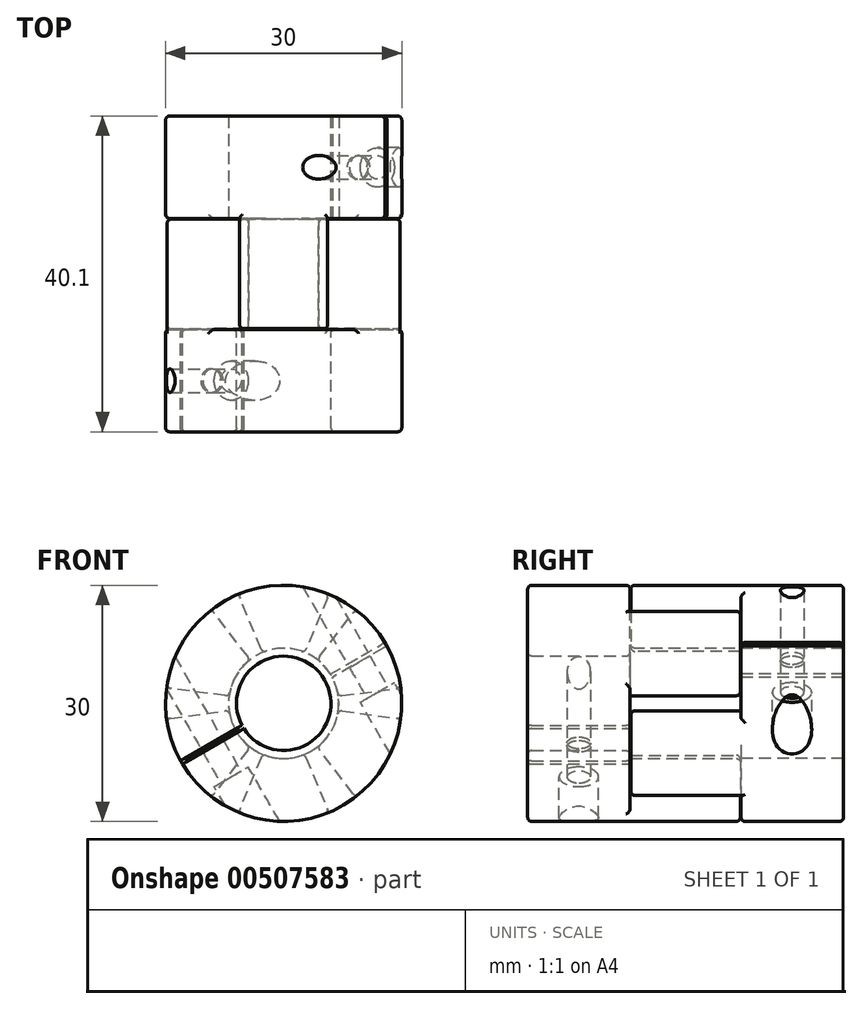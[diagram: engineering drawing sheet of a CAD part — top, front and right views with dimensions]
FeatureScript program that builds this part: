
annotation { "Feature Type Name" : "Feature", "Feature Type Description" : "" }
export const myFeature = defineFeature(function(context is Context, id is Id, definition is map)
    precondition{}
    {
        {
            var Q0;
            Q0=qCreatedBy(makeId("Front.planeOp"),FACE);
            var sketch = newSketch(context, id + "F0", { "sketchPlane" : qUnion([Q0])});
            skCircle(sketch, "E0", {"center": v(0, 0) * mm, "radius": 15 * mm});
            skSolve(sketch);
        }
        {
            var Q0;
            Q0=makeQuery(id+"F0.imprint","IMPRINT",FACE,{"disambiguationData":[TD([[makeQuery(id+"F0.imprint","IMPRINT",EDGE,{"derivedFrom":sQuery(id+"F0.wireOp",EDGE,"E0")}),1.0]])]});
            extrude(context, id + "F1", {"entities" : qUnion([Q0]), "depth" : 13 * mm});
        }
        {
            var Q0;
            Q0=makeQuery(id+"F1.opExtrude","CAP_FACE",FACE,{"disambiguationData":[OSD([sQuery(id+"F0.wireOp",EDGE,"E0")])],"isStart":false});
            var sketch = newSketch(context, id + "F2", { "sketchPlane" : qUnion([Q0])});
            skCircle(sketch, "E1", {"center": v(0, 0) * mm, "radius": 7 * mm});
            skSolve(sketch);
        }
        {
            var Q0;
            Q0=makeQuery(id+"F2.imprint","IMPRINT",FACE,{"disambiguationData":[TD([[makeQuery(id+"F2.imprint","IMPRINT",EDGE,{"derivedFrom":sQuery(id+"F2.wireOp",EDGE,"E1")}),1.0]])]});
            extrude(context, id + "F3", {"entities" : qUnion([Q0]), "operationType" : NewBodyOperationType.REMOVE, "oppositeDirection" : true, "depth" : 13 * mm});
        }
        {
            var Q0;
            Q0=makeQuery(id+"F1.opExtrude","CAP_FACE",FACE,{"disambiguationData":[OSD([sQuery(id+"F0.wireOp",EDGE,"E0")])],"isStart":false});
            var sketch = newSketch(context, id + "F4", { "sketchPlane" : qUnion([Q0])});
            skArc(sketch, "E2", {"start": v(2.68, 6.47) * mm, "mid": v(0, 7) * mm, "end": v(-2.68, 6.47) * mm});
            skArc(sketch, "E3", {"start": v(5.74, 13.86) * mm, "mid": v(0, 15) * mm, "end": v(-5.74, 13.86) * mm});
            skLineSegment(sketch, "E4", {"start": v(-2.68, 6.47) * mm, "end": v(-5.74, 13.86) * mm});
            skLineSegment(sketch, "E5", {"start": v(5.74, 13.86) * mm, "end": v(2.68, 6.47) * mm});
            skLineSegment(sketch, "E6.1.0", {"start": v(-4.26, -5.55) * mm, "end": v(-9.13, -11.9) * mm});
            skArc(sketch, "E6.1.1", {"start": v(-6.94, -0.91) * mm, "mid": v(-6.06, -3.5) * mm, "end": v(-4.26, -5.55) * mm});
            skArc(sketch, "E6.1.2", {"start": v(-14.87, -1.96) * mm, "mid": v(-13, -7.5) * mm, "end": v(-9.13, -11.9) * mm});
            skLineSegment(sketch, "E6.1.3", {"start": v(-14.87, -1.96) * mm, "end": v(-6.94, -0.91) * mm});
            skLineSegment(sketch, "E6.2.0", {"start": v(6.94, -0.91) * mm, "end": v(14.87, -1.96) * mm});
            skArc(sketch, "E6.2.1", {"start": v(4.26, -5.55) * mm, "mid": v(6.06, -3.5) * mm, "end": v(6.94, -0.91) * mm});
            skArc(sketch, "E6.2.2", {"start": v(9.13, -11.9) * mm, "mid": v(13, -7.5) * mm, "end": v(14.87, -1.96) * mm});
            skLineSegment(sketch, "E6.2.3", {"start": v(9.13, -11.9) * mm, "end": v(4.26, -5.55) * mm});
            skPoint(sketch, "E6.center", {"position": v(0, 0) * mm});
            skSolve(sketch);
        }
        {
            var Q0;
            Q0=makeQuery(id+"F4.imprint","IMPRINT",FACE,{"disambiguationData":[TD([[makeQuery(id+"F4.imprint","IMPRINT",EDGE,{"derivedFrom":sQuery(id+"F4.wireOp",EDGE,"E6.1.0")}),-1.0]])]});
            var Q1;
            Q1=makeQuery(id+"F4.imprint","IMPRINT",FACE,{"disambiguationData":[TD([[makeQuery(id+"F4.imprint","IMPRINT",EDGE,{"derivedFrom":sQuery(id+"F4.wireOp",EDGE,"E2")}),-1.0]])]});
            var Q2;
            Q2=makeQuery(id+"F4.imprint","IMPRINT",FACE,{"disambiguationData":[TD([[makeQuery(id+"F4.imprint","IMPRINT",EDGE,{"derivedFrom":sQuery(id+"F4.wireOp",EDGE,"E6.2.0")}),-1.0]])]});
            extrude(context, id + "F5", {"entities" : qUnion([Q0, Q1, Q2]), "operationType" : NewBodyOperationType.ADD, "depth" : 14 * mm});
        }
        {
            var Q0;
            Q0=makeQuery(id+"F5.opExtrude","CAP_EDGE",EDGE,{"disambiguationData":[OSD([sQuery(id+"F4.wireOp",EDGE,"E6.1.2")])],"isStart":false});
            var Q1;
            Q1=makeQuery(id+"F5.opExtrude","CAP_EDGE",EDGE,{"disambiguationData":[OSD([sQuery(id+"F4.wireOp",EDGE,"E6.1.0")])],"isStart":false});
            var Q2;
            Q2=makeQuery(id+"F5.opExtrude","CAP_EDGE",EDGE,{"disambiguationData":[OSD([sQuery(id+"F4.wireOp",EDGE,"E6.1.1")])],"isStart":false});
            var Q3;
            Q3=makeQuery(id+"F5.opExtrude","CAP_EDGE",EDGE,{"disambiguationData":[OSD([sQuery(id+"F4.wireOp",EDGE,"E6.1.3")])],"isStart":false});
            var Q4;
            Q4=makeQuery(id+"F5.opExtrude","SWEPT_EDGE",EDGE,{"disambiguationData":[OSD([sQuery(id+"F0.wireOp",EDGE,"E0"),sQuery(id+"F4.wireOp",EDGE,"E6.1.0"),sQuery(id+"F4.wireOp",EDGE,"E6.1.2")])]});
            var Q5;
            Q5=makeQuery(id+"F5.opExtrude","SWEPT_EDGE",EDGE,{"disambiguationData":[OSD([sQuery(id+"F0.wireOp",EDGE,"E0"),sQuery(id+"F4.wireOp",EDGE,"E6.1.2"),sQuery(id+"F4.wireOp",EDGE,"E6.1.3")])]});
            var Q6;
            Q6=makeQuery(id+"F5.opExtrude","SWEPT_EDGE",EDGE,{"disambiguationData":[OSD([sQuery(id+"F2.wireOp",EDGE,"E1"),sQuery(id+"F4.wireOp",EDGE,"E6.1.1"),sQuery(id+"F4.wireOp",EDGE,"E6.1.3")])]});
            var Q7;
            Q7=makeQuery(id+"F5.opExtrude","SWEPT_EDGE",EDGE,{"disambiguationData":[OSD([sQuery(id+"F2.wireOp",EDGE,"E1"),sQuery(id+"F4.wireOp",EDGE,"E6.1.0"),sQuery(id+"F4.wireOp",EDGE,"E6.1.1")])]});
            var Q8;
            {var subQ0=sQuery(id+"F2.wireOp",EDGE,"E1");Q8=makeQuery(id+"F5.boolean.opBoolean","SPLIT",EDGE,{"disambiguationData":[TD([makeQuery(id+"F5.opExtrude","SWEPT_FACE",FACE,{"disambiguationData":[OSD([sQuery(id+"F4.wireOp",EDGE,"E6.1.0")])]})])],"derivedFrom":makeQuery(id+"F3.boolean.opBoolean","COPY",EDGE,{"derivedFrom":makeQuery(id+"F3.opExtrude","CAP_EDGE",EDGE,{"disambiguationData":[OSD([subQ0])],"isStart":true})})});}
            var Q9;
            {var subQ0=sQuery(id+"F0.wireOp",EDGE,"E0");Q9=makeQuery(id+"F5.boolean.opBoolean","SPLIT",EDGE,{"disambiguationData":[TD([makeQuery(id+"F5.opExtrude","SWEPT_FACE",FACE,{"disambiguationData":[OSD([sQuery(id+"F4.wireOp",EDGE,"E6.1.0")])]})])],"derivedFrom":makeQuery(id+"F1.opExtrude","CAP_EDGE",EDGE,{"disambiguationData":[OSD([subQ0])],"isStart":false})});}
            var Q10;
            Q10=makeQuery(id+"F5.opExtrude","SWEPT_EDGE",EDGE,{"disambiguationData":[OSD([sQuery(id+"F2.wireOp",EDGE,"E1"),sQuery(id+"F4.wireOp",EDGE,"E6.2.1"),sQuery(id+"F4.wireOp",EDGE,"E6.2.3")])]});
            var Q11;
            Q11=makeQuery(id+"F5.opExtrude","CAP_EDGE",EDGE,{"disambiguationData":[OSD([sQuery(id+"F4.wireOp",EDGE,"E6.2.3")])],"isStart":false});
            var Q12;
            Q12=makeQuery(id+"F5.opExtrude","SWEPT_EDGE",EDGE,{"disambiguationData":[OSD([sQuery(id+"F0.wireOp",EDGE,"E0"),sQuery(id+"F4.wireOp",EDGE,"E6.2.2"),sQuery(id+"F4.wireOp",EDGE,"E6.2.3")])]});
            var Q13;
            Q13=makeQuery(id+"F5.opExtrude","CAP_EDGE",EDGE,{"disambiguationData":[OSD([sQuery(id+"F4.wireOp",EDGE,"E6.2.1")])],"isStart":false});
            var Q14;
            Q14=makeQuery(id+"F5.opExtrude","CAP_EDGE",EDGE,{"disambiguationData":[OSD([sQuery(id+"F4.wireOp",EDGE,"E6.2.2")])],"isStart":false});
            var Q15;
            Q15=makeQuery(id+"F5.opExtrude","SWEPT_EDGE",EDGE,{"disambiguationData":[OSD([sQuery(id+"F0.wireOp",EDGE,"E0"),sQuery(id+"F4.wireOp",EDGE,"E6.2.0"),sQuery(id+"F4.wireOp",EDGE,"E6.2.2")])]});
            var Q16;
            Q16=makeQuery(id+"F5.opExtrude","CAP_EDGE",EDGE,{"disambiguationData":[OSD([sQuery(id+"F4.wireOp",EDGE,"E6.2.0")])],"isStart":false});
            var Q17;
            Q17=makeQuery(id+"F5.opExtrude","SWEPT_EDGE",EDGE,{"disambiguationData":[OSD([sQuery(id+"F2.wireOp",EDGE,"E1"),sQuery(id+"F4.wireOp",EDGE,"E6.2.0"),sQuery(id+"F4.wireOp",EDGE,"E6.2.1")])]});
            var Q18;
            {var subQ0=sQuery(id+"F2.wireOp",EDGE,"E1");Q18=makeQuery(id+"F5.boolean.opBoolean","SPLIT",EDGE,{"disambiguationData":[TD([makeQuery(id+"F5.opExtrude","SWEPT_FACE",FACE,{"disambiguationData":[OSD([sQuery(id+"F4.wireOp",EDGE,"E5")])]})])],"derivedFrom":makeQuery(id+"F3.boolean.opBoolean","COPY",EDGE,{"derivedFrom":makeQuery(id+"F3.opExtrude","CAP_EDGE",EDGE,{"disambiguationData":[OSD([subQ0])],"isStart":true})})});}
            var Q19;
            {var subQ0=sQuery(id+"F0.wireOp",EDGE,"E0");Q19=makeQuery(id+"F5.boolean.opBoolean","SPLIT",EDGE,{"disambiguationData":[TD([makeQuery(id+"F5.opExtrude","SWEPT_FACE",FACE,{"disambiguationData":[OSD([sQuery(id+"F4.wireOp",EDGE,"E5")])]})])],"derivedFrom":makeQuery(id+"F1.opExtrude","CAP_EDGE",EDGE,{"disambiguationData":[OSD([subQ0])],"isStart":false})});}
            var Q20;
            Q20=makeQuery(id+"F5.opExtrude","SWEPT_EDGE",EDGE,{"disambiguationData":[OSD([sQuery(id+"F2.wireOp",EDGE,"E1"),sQuery(id+"F4.wireOp",EDGE,"E2"),sQuery(id+"F4.wireOp",EDGE,"E5")])]});
            var Q21;
            Q21=makeQuery(id+"F5.opExtrude","SWEPT_EDGE",EDGE,{"disambiguationData":[OSD([sQuery(id+"F0.wireOp",EDGE,"E0"),sQuery(id+"F4.wireOp",EDGE,"E3"),sQuery(id+"F4.wireOp",EDGE,"E5")])]});
            var Q22;
            Q22=makeQuery(id+"F5.opExtrude","CAP_EDGE",EDGE,{"disambiguationData":[OSD([sQuery(id+"F4.wireOp",EDGE,"E5")])],"isStart":false});
            var Q23;
            Q23=makeQuery(id+"F5.opExtrude","CAP_EDGE",EDGE,{"disambiguationData":[OSD([sQuery(id+"F4.wireOp",EDGE,"E2")])],"isStart":false});
            var Q24;
            Q24=makeQuery(id+"F5.opExtrude","CAP_EDGE",EDGE,{"disambiguationData":[OSD([sQuery(id+"F4.wireOp",EDGE,"E4")])],"isStart":false});
            var Q25;
            Q25=makeQuery(id+"F5.opExtrude","CAP_EDGE",EDGE,{"disambiguationData":[OSD([sQuery(id+"F4.wireOp",EDGE,"E3")])],"isStart":false});
            var Q26;
            Q26=makeQuery(id+"F5.opExtrude","SWEPT_EDGE",EDGE,{"disambiguationData":[OSD([sQuery(id+"F2.wireOp",EDGE,"E1"),sQuery(id+"F4.wireOp",EDGE,"E2"),sQuery(id+"F4.wireOp",EDGE,"E4")])]});
            var Q27;
            Q27=makeQuery(id+"F5.opExtrude","SWEPT_EDGE",EDGE,{"disambiguationData":[OSD([sQuery(id+"F0.wireOp",EDGE,"E0"),sQuery(id+"F4.wireOp",EDGE,"E3"),sQuery(id+"F4.wireOp",EDGE,"E4")])]});
            var Q28;
            {var subQ0=sQuery(id+"F0.wireOp",EDGE,"E0");Q28=makeQuery(id+"F5.boolean.opBoolean","SPLIT",EDGE,{"disambiguationData":[TD([makeQuery(id+"F5.opExtrude","SWEPT_FACE",FACE,{"disambiguationData":[OSD([sQuery(id+"F4.wireOp",EDGE,"E4")])]})])],"derivedFrom":makeQuery(id+"F1.opExtrude","CAP_EDGE",EDGE,{"disambiguationData":[OSD([subQ0])],"isStart":false})});}
            var Q29;
            {var subQ0=sQuery(id+"F2.wireOp",EDGE,"E1");Q29=makeQuery(id+"F5.boolean.opBoolean","SPLIT",EDGE,{"disambiguationData":[TD([makeQuery(id+"F5.opExtrude","SWEPT_FACE",FACE,{"disambiguationData":[OSD([sQuery(id+"F4.wireOp",EDGE,"E4")])]})])],"derivedFrom":makeQuery(id+"F3.boolean.opBoolean","COPY",EDGE,{"derivedFrom":makeQuery(id+"F3.opExtrude","CAP_EDGE",EDGE,{"disambiguationData":[OSD([subQ0])],"isStart":true})})});}
            fillet(context, id + "F6", {"entities" : qUnion([Q0, Q1, Q2, Q3, Q4, Q5, Q6, Q7, Q8, Q9, Q10, Q11, Q12, Q13, Q14, Q15, Q16, Q17, Q18, Q19, Q20, Q21, Q22, Q23, Q24, Q25, Q26, Q27, Q28, Q29]), "radius" : 0.5 * mm, "tangentPropagation" : true, "allowEdgeOverflow" : false});
        }
        {
            var Q0;
            Q0=makeQuery(id+"F3.boolean.opBoolean","COPY",EDGE,{"derivedFrom":makeQuery(id+"F3.opExtrude","CAP_EDGE",EDGE,{"disambiguationData":[OSD([sQuery(id+"F2.wireOp",EDGE,"E1")])],"isStart":false})});
            var Q1;
            Q1=makeQuery(id+"F1.opExtrude","CAP_EDGE",EDGE,{"disambiguationData":[OSD([sQuery(id+"F0.wireOp",EDGE,"E0")])],"isStart":true});
            fillet(context, id + "F7", {"entities" : qUnion([Q0, Q1]), "radius" : 0.5 * mm, "tangentPropagation" : true, "allowEdgeOverflow" : false});
        }
        {
            var Q0;
            {var subQ0=sQuery(id+"F0.wireOp",EDGE,"E0");Q0=makeQuery(id+"F5.boolean.opBoolean","SPLIT",FACE,{"disambiguationData":[TD([makeQuery(id+"F5.opExtrude","SWEPT_FACE",FACE,{"disambiguationData":[OSD([sQuery(id+"F4.wireOp",EDGE,"E5")])]})])],"derivedFrom":makeQuery(id+"F1.opExtrude","CAP_FACE",FACE,{"disambiguationData":[OSD([subQ0])],"isStart":false})});}
            var sketch = newSketch(context, id + "F8", { "sketchPlane" : qUnion([Q0])});
            skLineSegment(sketch, "E7", {"start": v(0, 0) * mm, "end": v(4.34, 2.5) * mm});
            skLineSegment(sketch, "E8", {"start": v(13.7, 7.91) * mm, "end": v(13.83, 7.7) * mm});
            skLineSegment(sketch, "E9", {"start": v(13.83, 7.7) * mm, "end": v(13.58, 8.13) * mm});
            skLineSegment(sketch, "E10", {"start": v(7.44, -0.98) * mm, "end": v(14.38, -1.9) * mm});
            skLineSegment(sketch, "E11", {"start": v(14.38, -1.9) * mm, "end": v(10.09, 5.54) * mm});
            skLineSegment(sketch, "E12", {"start": v(5.55, 13.4) * mm, "end": v(2.87, 6.93) * mm});
            skLineSegment(sketch, "E13", {"start": v(13.83, 7.7) * mm, "end": v(4.46, 2.29) * mm});
            skLineSegment(sketch, "E14", {"start": v(4.21, 2.72) * mm, "end": v(13.58, 8.13) * mm});
            skLineSegment(sketch, "E15", {"start": v(4.21, 2.72) * mm, "end": v(4.46, 2.29) * mm});
            skLineSegment(sketch, "E16.trimOffspring", {"start": v(9.84, 5.97) * mm, "end": v(5.55, 13.4) * mm});
            skSolve(sketch);
        }
        {
            var Q0;
            {var subQ20=sQuery(id+"F8.wireOp",EDGE,"E13");var subQ22=makeQuery(id+"F8.imprint","INTERSECT",VERTEX,{"derivedFrom":[sQuery(id+"F8.wireOp",EDGE,"E11"),subQ20]});Q0=makeQuery(id+"F8.imprint","IMPRINT",FACE,{"disambiguationData":[TD([[makeQuery(id+"F8.imprint","IMPRINT",EDGE,{"disambiguationData":[TD([[subQ22,1.0]])],"derivedFrom":subQ20}),-1.0]])]});}
            var Q1;
            {var subQ0=sQuery(id+"F8.wireOp",EDGE,"E13");var subQ1=sQuery(id+"F8.wireOp",EDGE,"E9");var subQ2=makeQuery(id+"F8.imprint","INTERSECT",VERTEX,{"derivedFrom":[subQ1,subQ0]});Q1=makeQuery(id+"F8.imprint","IMPRINT",FACE,{"disambiguationData":[TD([[makeQuery(id+"F8.imprint","IMPRINT",EDGE,{"disambiguationData":[TD([[subQ2,-1.0]])],"derivedFrom":subQ1}),1.0]])]});}
            var Q2;
            {var subQ0=sQuery(id+"F8.wireOp",EDGE,"E15");var subQ1=makeQuery(id+"F8.imprint","IMPRINT",VERTEX,{"derivedFrom":subQ0});Q2=makeQuery(id+"F8.imprint","IMPRINT",FACE,{"disambiguationData":[TD([[makeQuery(id+"F8.imprint","IMPRINT",EDGE,{"disambiguationData":[TD([[subQ1,1.0]])],"derivedFrom":subQ0}),1.0]])]});}
            extrude(context, id + "F9", {"entities" : qUnion([Q0, Q1, Q2]), "operationType" : NewBodyOperationType.REMOVE, "oppositeDirection" : true, "depth" : 13 * mm});
        }
        {
            var Q0;
            Q0=makeQuery(id+"F9.boolean.opBoolean","COPY",FACE,{"derivedFrom":makeQuery(id+"F9.opExtrude","SWEPT_FACE",FACE,{"disambiguationData":[OSD([sQuery(id+"F8.wireOp",EDGE,"E14")])]})});
            var sketch = newSketch(context, id + "F10", { "sketchPlane" : qUnion([Q0])});
            skLineSegment(sketch, "E17.bottom", {"start": v(7.5, 0) * mm, "end": v(14.5, 0) * mm});
            skLineSegment(sketch, "E17.top", {"start": v(7.5, 13) * mm, "end": v(14.5, 13) * mm});
            skLineSegment(sketch, "E17.left", {"start": v(7.5, 0) * mm, "end": v(7.5, 13) * mm});
            skLineSegment(sketch, "E17.right", {"start": v(14.5, 0) * mm, "end": v(14.5, 13) * mm});
            skCircle(sketch, "E18", {"center": v(11, 6.5) * mm, "radius": 1.5 * mm});
            skSolve(sketch);
        }
        {
            var Q0;
            Q0=makeQuery(id+"F10.imprint","IMPRINT",FACE,{"disambiguationData":[TD([[makeQuery(id+"F10.imprint","IMPRINT",EDGE,{"derivedFrom":sQuery(id+"F10.wireOp",EDGE,"E18")}),1.0]])]});
            extrude(context, id + "F11", {"entities" : qUnion([Q0]), "operationType" : NewBodyOperationType.REMOVE, "oppositeDirection" : true, "depth" : 25 * mm, "symmetric" : true});
        }
        {
            var Q0;
            Q0=makeQuery(id+"F9.boolean.opBoolean","COPY",FACE,{"derivedFrom":makeQuery(id+"F9.opExtrude","SWEPT_FACE",FACE,{"disambiguationData":[OSD([sQuery(id+"F8.wireOp",EDGE,"E14")])]})});
            cPlane(context, id + "F12", {"entities" : qUnion([Q0]), "cplaneType" : CPlaneType.OFFSET, "offset" : 5 * mm, "width" : 150 * mm, "height" : 150 * mm});
        }
        {
            var Q0;
            Q0=qCreatedBy(id+"F12.planeOp",FACE);
            var sketch = newSketch(context, id + "F13", { "sketchPlane" : qUnion([Q0])});
            skCircle(sketch, "E19", {"center": v(11, 6.53) * mm, "radius": 2.5 * mm});
            skSolve(sketch);
        }
        {
            var Q0;
            Q0=makeQuery(id+"F13.imprint","IMPRINT",FACE,{"disambiguationData":[TD([[makeQuery(id+"F13.imprint","IMPRINT",EDGE,{"derivedFrom":sQuery(id+"F13.wireOp",EDGE,"E19")}),1.0]])]});
            extrude(context, id + "F14", {"entities" : qUnion([Q0]), "operationType" : NewBodyOperationType.REMOVE, "depth" : 25 * mm});
        }
        {
            var Q0;
            {var subQ0=makeQuery(id+"F5.opExtrude","SWEPT_FACE",FACE,{"disambiguationData":[OSD([sQuery(id+"F4.wireOp",EDGE,"E5")])]});var subQ5=sQuery(id+"F0.wireOp",EDGE,"E0");var subQ6=makeQuery(id+"F1.opExtrude","CAP_FACE",FACE,{"disambiguationData":[OSD([subQ5])],"isStart":false});var subQ8=sQuery(id+"F4.wireOp",EDGE,"E6.2.0");var subQ9=makeQuery(id+"F5.opExtrude","SWEPT_FACE",FACE,{"disambiguationData":[OSD([subQ8])]});Q0=makeQuery(id+"F9.boolean.opBoolean","SPLIT",FACE,{"disambiguationData":[TD([subQ9])],"derivedFrom":makeQuery(id+"F5.boolean.opBoolean","SPLIT",FACE,{"disambiguationData":[TD([subQ0])],"derivedFrom":subQ6})});}
            cPlane(context, id + "F15", {"entities" : qUnion([Q0]), "cplaneType" : CPlaneType.OFFSET, "offset" : 0.1 * mm, "width" : 150 * mm, "height" : 150 * mm});
        }
        {
            var Q0;
            Q0=qCreatedBy(id+"F15.planeOp",FACE);
            var sketch = newSketch(context, id + "F16", { "sketchPlane" : qUnion([Q0])});
            skLineSegment(sketch, "E20", {"start": v(-2.68, -6.47) * mm, "end": v(-5.74, -13.86) * mm});
            skLineSegment(sketch, "E21", {"start": v(2.68, -6.47) * mm, "end": v(5.74, -13.86) * mm});
            skLineSegment(sketch, "E22", {"start": v(0, 0) * mm, "end": v(0, -7) * mm});
            skArc(sketch, "E23", {"start": v(-2.68, -6.47) * mm, "mid": v(0, -7) * mm, "end": v(2.68, -6.47) * mm});
            skArc(sketch, "E24", {"start": v(-5.74, -13.86) * mm, "mid": v(0, -15) * mm, "end": v(5.74, -13.86) * mm});
            skLineSegment(sketch, "E25.1.0", {"start": v(6.94, 0.91) * mm, "end": v(14.87, 1.96) * mm});
            skArc(sketch, "E25.1.1", {"start": v(6.94, 0.91) * mm, "mid": v(6.06, 3.5) * mm, "end": v(4.26, 5.55) * mm});
            skLineSegment(sketch, "E25.1.2", {"start": v(4.26, 5.55) * mm, "end": v(9.13, 11.9) * mm});
            skArc(sketch, "E25.1.3", {"start": v(14.87, 1.96) * mm, "mid": v(13, 7.5) * mm, "end": v(9.13, 11.9) * mm});
            skLineSegment(sketch, "E25.2.0", {"start": v(-4.26, 5.55) * mm, "end": v(-9.13, 11.9) * mm});
            skArc(sketch, "E25.2.1", {"start": v(-4.26, 5.55) * mm, "mid": v(-6.06, 3.5) * mm, "end": v(-6.94, 0.91) * mm});
            skLineSegment(sketch, "E25.2.2", {"start": v(-6.94, 0.91) * mm, "end": v(-14.87, 1.96) * mm});
            skArc(sketch, "E25.2.3", {"start": v(-9.13, 11.9) * mm, "mid": v(-13, 7.5) * mm, "end": v(-14.87, 1.96) * mm});
            skPoint(sketch, "E25.center", {"position": v(0, 0) * mm});
            skSolve(sketch);
        }
        {
            var Q0;
            Q0=makeQuery(id+"F16.imprint","IMPRINT",FACE,{"disambiguationData":[TD([[makeQuery(id+"F16.imprint","IMPRINT",EDGE,{"derivedFrom":sQuery(id+"F16.wireOp",EDGE,"E25.2.0")}),1.0]])]});
            var Q1;
            {var subQ3=sQuery(id+"F16.wireOp",EDGE,"E20");Q1=makeQuery(id+"F16.imprint","IMPRINT",FACE,{"disambiguationData":[TD([[makeQuery(id+"F16.imprint","IMPRINT",EDGE,{"derivedFrom":subQ3}),1.0]])]});}
            var Q2;
            Q2=makeQuery(id+"F16.imprint","IMPRINT",FACE,{"disambiguationData":[TD([[makeQuery(id+"F16.imprint","IMPRINT",EDGE,{"derivedFrom":sQuery(id+"F16.wireOp",EDGE,"E25.1.0")}),1.0]])]});
            extrude(context, id + "F17", {"entities" : qUnion([Q0, Q1, Q2]), "depth" : 14 * mm});
        }
        {
            var Q0;
            Q0=makeQuery(id+"F17.opExtrude","CAP_FACE",FACE,{"disambiguationData":[OSD([sQuery(id+"F16.wireOp",EDGE,"E25.1.0"),sQuery(id+"F16.wireOp",EDGE,"E25.1.1"),sQuery(id+"F16.wireOp",EDGE,"E25.1.2"),sQuery(id+"F16.wireOp",EDGE,"E25.1.3")])],"isStart":false});
            var sketch = newSketch(context, id + "F18", { "sketchPlane" : qUnion([Q0])});
            skCircle(sketch, "E26", {"center": v(0, 0) * mm, "radius": 6 * mm});
            skCircle(sketch, "E27", {"center": v(0, 0) * mm, "radius": 15 * mm});
            skSolve(sketch);
        }
        {
            var Q0;
            {var subQ1=makeQuery(id+"F17.opExtrude","CAP_EDGE",EDGE,{"disambiguationData":[OSD([sQuery(id+"F16.wireOp",EDGE,"E25.1.0")])],"isStart":false});Q0=makeQuery(id+"F18.imprint","IMPRINT",FACE,{"disambiguationData":[TD([[makeQuery(id+"F18.imprint","IMPRINT",EDGE,{"derivedFrom":subQ1}),-1.0]])]});}
            var Q1;
            {var subQ1=makeQuery(id+"F17.opExtrude","CAP_EDGE",EDGE,{"disambiguationData":[OSD([sQuery(id+"F16.wireOp",EDGE,"E25.1.0")])],"isStart":false});Q1=makeQuery(id+"F18.imprint","IMPRINT",FACE,{"disambiguationData":[TD([[makeQuery(id+"F18.imprint","IMPRINT",EDGE,{"derivedFrom":subQ1}),1.0]])]});}
            extrude(context, id + "F19", {"entities" : qUnion([Q0, Q1]), "operationType" : NewBodyOperationType.ADD, "depth" : 13 * mm});
        }
        {
            var Q0;
            {var subQ0=sQuery(id+"F18.wireOp",EDGE,"E27");Q0=makeQuery(id+"F19.boolean.opBoolean","SPLIT",EDGE,{"disambiguationData":[TD([makeQuery(id+"F17.opExtrude","SWEPT_FACE",FACE,{"disambiguationData":[OSD([sQuery(id+"F16.wireOp",EDGE,"E21")])]})])],"derivedFrom":makeQuery(id+"F19.opExtrude","CAP_EDGE",EDGE,{"disambiguationData":[OSD([subQ0])],"isStart":true})});}
            var Q1;
            Q1=makeQuery(id+"F17.opExtrude","SWEPT_EDGE",EDGE,{"disambiguationData":[OSD([sQuery(id+"F16.wireOp",EDGE,"E21"),sQuery(id+"F16.wireOp",EDGE,"E24")])]});
            var Q2;
            Q2=makeQuery(id+"F17.opExtrude","CAP_EDGE",EDGE,{"disambiguationData":[OSD([sQuery(id+"F16.wireOp",EDGE,"E21")])],"isStart":true});
            var Q3;
            Q3=makeQuery(id+"F17.opExtrude","CAP_EDGE",EDGE,{"disambiguationData":[OSD([sQuery(id+"F16.wireOp",EDGE,"E23")])],"isStart":true});
            var Q4;
            Q4=makeQuery(id+"F17.opExtrude","CAP_EDGE",EDGE,{"disambiguationData":[OSD([sQuery(id+"F16.wireOp",EDGE,"E20")])],"isStart":true});
            var Q5;
            Q5=makeQuery(id+"F17.opExtrude","CAP_EDGE",EDGE,{"disambiguationData":[OSD([sQuery(id+"F16.wireOp",EDGE,"E24")])],"isStart":true});
            var Q6;
            Q6=makeQuery(id+"F17.opExtrude","SWEPT_EDGE",EDGE,{"disambiguationData":[OSD([sQuery(id+"F16.wireOp",EDGE,"E20"),sQuery(id+"F16.wireOp",EDGE,"E24")])]});
            var Q7;
            {var subQ0=sQuery(id+"F18.wireOp",EDGE,"E27");Q7=makeQuery(id+"F19.boolean.opBoolean","SPLIT",EDGE,{"disambiguationData":[TD([makeQuery(id+"F17.opExtrude","SWEPT_FACE",FACE,{"disambiguationData":[OSD([sQuery(id+"F16.wireOp",EDGE,"E20")])]})])],"derivedFrom":makeQuery(id+"F19.opExtrude","CAP_EDGE",EDGE,{"disambiguationData":[OSD([subQ0])],"isStart":true})});}
            var Q8;
            Q8=makeQuery(id+"F17.opExtrude","SWEPT_EDGE",EDGE,{"disambiguationData":[OSD([sQuery(id+"F16.wireOp",EDGE,"E25.2.2"),sQuery(id+"F16.wireOp",EDGE,"E25.2.3")])]});
            var Q9;
            Q9=makeQuery(id+"F17.opExtrude","CAP_EDGE",EDGE,{"disambiguationData":[OSD([sQuery(id+"F16.wireOp",EDGE,"E25.2.2")])],"isStart":true});
            var Q10;
            Q10=makeQuery(id+"F17.opExtrude","CAP_EDGE",EDGE,{"disambiguationData":[OSD([sQuery(id+"F16.wireOp",EDGE,"E25.2.1")])],"isStart":true});
            var Q11;
            Q11=makeQuery(id+"F17.opExtrude","CAP_EDGE",EDGE,{"disambiguationData":[OSD([sQuery(id+"F16.wireOp",EDGE,"E25.2.0")])],"isStart":true});
            var Q12;
            Q12=makeQuery(id+"F17.opExtrude","CAP_EDGE",EDGE,{"disambiguationData":[OSD([sQuery(id+"F16.wireOp",EDGE,"E25.2.3")])],"isStart":true});
            var Q13;
            Q13=makeQuery(id+"F17.opExtrude","SWEPT_EDGE",EDGE,{"disambiguationData":[OSD([sQuery(id+"F16.wireOp",EDGE,"E25.1.0"),sQuery(id+"F16.wireOp",EDGE,"E25.1.3")])]});
            var Q14;
            Q14=makeQuery(id+"F17.opExtrude","CAP_EDGE",EDGE,{"disambiguationData":[OSD([sQuery(id+"F16.wireOp",EDGE,"E25.1.0")])],"isStart":true});
            var Q15;
            Q15=makeQuery(id+"F17.opExtrude","SWEPT_EDGE",EDGE,{"disambiguationData":[OSD([sQuery(id+"F16.wireOp",EDGE,"E25.1.0"),sQuery(id+"F16.wireOp",EDGE,"E25.1.1")])]});
            var Q16;
            Q16=makeQuery(id+"F17.opExtrude","CAP_EDGE",EDGE,{"disambiguationData":[OSD([sQuery(id+"F16.wireOp",EDGE,"E25.1.1")])],"isStart":true});
            var Q17;
            Q17=makeQuery(id+"F17.opExtrude","CAP_EDGE",EDGE,{"disambiguationData":[OSD([sQuery(id+"F16.wireOp",EDGE,"E25.1.3")])],"isStart":true});
            var Q18;
            Q18=makeQuery(id+"F17.opExtrude","CAP_EDGE",EDGE,{"disambiguationData":[OSD([sQuery(id+"F16.wireOp",EDGE,"E25.1.2")])],"isStart":true});
            var Q19;
            Q19=makeQuery(id+"F17.opExtrude","SWEPT_EDGE",EDGE,{"disambiguationData":[OSD([sQuery(id+"F16.wireOp",EDGE,"E25.2.1"),sQuery(id+"F16.wireOp",EDGE,"E25.2.2")])]});
            var Q20;
            Q20=makeQuery(id+"F17.opExtrude","SWEPT_EDGE",EDGE,{"disambiguationData":[OSD([sQuery(id+"F16.wireOp",EDGE,"E21"),sQuery(id+"F16.wireOp",EDGE,"E23")])]});
            var Q21;
            Q21=makeQuery(id+"F17.opExtrude","SWEPT_EDGE",EDGE,{"disambiguationData":[OSD([sQuery(id+"F16.wireOp",EDGE,"E20"),sQuery(id+"F16.wireOp",EDGE,"E23")])]});
            var Q22;
            Q22=makeQuery(id+"F17.opExtrude","SWEPT_EDGE",EDGE,{"disambiguationData":[OSD([sQuery(id+"F16.wireOp",EDGE,"E25.1.1"),sQuery(id+"F16.wireOp",EDGE,"E25.1.2")])]});
            var Q23;
            Q23=makeQuery(id+"F17.opExtrude","SWEPT_EDGE",EDGE,{"disambiguationData":[OSD([sQuery(id+"F16.wireOp",EDGE,"E25.2.0"),sQuery(id+"F16.wireOp",EDGE,"E25.2.1")])]});
            var Q24;
            Q24=makeQuery(id+"F17.opExtrude","SWEPT_EDGE",EDGE,{"disambiguationData":[OSD([sQuery(id+"F16.wireOp",EDGE,"E25.2.0"),sQuery(id+"F16.wireOp",EDGE,"E25.2.3")])]});
            var Q25;
            Q25=makeQuery(id+"F17.opExtrude","SWEPT_EDGE",EDGE,{"disambiguationData":[OSD([sQuery(id+"F16.wireOp",EDGE,"E25.1.2"),sQuery(id+"F16.wireOp",EDGE,"E25.1.3")])]});
            var Q26;
            {var subQ0=sQuery(id+"F18.wireOp",EDGE,"E27");Q26=makeQuery(id+"F19.boolean.opBoolean","SPLIT",EDGE,{"disambiguationData":[TD([makeQuery(id+"F17.opExtrude","SWEPT_FACE",FACE,{"disambiguationData":[OSD([sQuery(id+"F16.wireOp",EDGE,"E25.1.2")])]})])],"derivedFrom":makeQuery(id+"F19.opExtrude","CAP_EDGE",EDGE,{"disambiguationData":[OSD([subQ0])],"isStart":true})});}
            var Q27;
            Q27=makeQuery(id+"F19.opExtrude","CAP_EDGE",EDGE,{"disambiguationData":[OSD([sQuery(id+"F18.wireOp",EDGE,"E26")])],"isStart":true});
            var Q28;
            Q28=makeQuery(id+"F19.opExtrude","CAP_EDGE",EDGE,{"disambiguationData":[OSD([sQuery(id+"F18.wireOp",EDGE,"E26")])],"isStart":false});
            var Q29;
            Q29=makeQuery(id+"F19.opExtrude","CAP_EDGE",EDGE,{"disambiguationData":[OSD([sQuery(id+"F18.wireOp",EDGE,"E27")])],"isStart":false});
            fillet(context, id + "F20", {"entities" : qUnion([Q0, Q1, Q2, Q3, Q4, Q5, Q6, Q7, Q8, Q9, Q10, Q11, Q12, Q13, Q14, Q15, Q16, Q17, Q18, Q19, Q20, Q21, Q22, Q23, Q24, Q25, Q26, Q27, Q28, Q29]), "radius" : 0.5 * mm, "tangentPropagation" : true, "allowEdgeOverflow" : false});
        }
        {
            var Q0;
            Q0=makeQuery(id+"F19.opExtrude","CAP_FACE",FACE,{"disambiguationData":[OSD([sQuery(id+"F18.wireOp",EDGE,"E26"),sQuery(id+"F18.wireOp",EDGE,"E27")])],"isStart":true});
            var sketch = newSketch(context, id + "F21", { "sketchPlane" : qUnion([Q0])});
            skLineSegment(sketch, "E28", {"start": v(0, 0) * mm, "end": v(19.31, -11.15) * mm});
            skLineSegment(sketch, "E29", {"start": v(2.86, -6.91) * mm, "end": v(5.55, -13.4) * mm});
            skLineSegment(sketch, "E30", {"start": v(7.42, 0.98) * mm, "end": v(14.38, 1.9) * mm});
            skLineSegment(sketch, "E31", {"start": v(14.18, -8.19) * mm, "end": v(12.89, -10.43) * mm});
            skLineSegment(sketch, "E32", {"start": v(12.89, -10.43) * mm, "end": v(15.35, -6.16) * mm});
            skLineSegment(sketch, "E33", {"start": v(13.97, -7.78) * mm, "end": v(3.16, -1.53) * mm});
            skLineSegment(sketch, "E34", {"start": v(13.72, -8.21) * mm, "end": v(2.9, -1.97) * mm});
            skLineSegment(sketch, "E35", {"start": v(13.97, -7.78) * mm, "end": v(13.72, -8.21) * mm});
            skLineSegment(sketch, "E36", {"start": v(3.16, -1.53) * mm, "end": v(2.9, -1.97) * mm});
            skArc(sketch, "E37", {"start": v(5.07, -3.21) * mm, "mid": v(5.2, -3) * mm, "end": v(5.32, -2.78) * mm});
            skArc(sketch, "E38", {"start": v(12.86, -7.72) * mm, "mid": v(13, -7.5) * mm, "end": v(13.11, -7.28) * mm});
            skSolve(sketch);
        }
        {
            var Q0;
            {var subQ0=sQuery(id+"F21.wireOp",EDGE,"E28");var subQ1=sQuery(id+"F18.wireOp",EDGE,"E27");var subQ2=sQuery(id+"F18.wireOp",EDGE,"E26");var subQ3=makeQuery(id+"F19.opExtrude","CAP_FACE",FACE,{"disambiguationData":[OSD([subQ2,subQ1])],"isStart":true});var subQ4=subQ3;var subQ7=makeQuery(id+"F20.opFillet","BLEND_EDGE",EDGE,{"blendedFrom":[makeQuery(id+"F19.opExtrude","CAP_EDGE",EDGE,{"disambiguationData":[OSD([subQ2])],"isStart":true}),subQ4],"blendedInto":[subQ4]});var subQ8=makeQuery(id+"F21.imprint","INTERSECT",VERTEX,{"derivedFrom":[subQ7,subQ0]});Q0=makeQuery(id+"F21.imprint","IMPRINT",FACE,{"disambiguationData":[TD([[makeQuery(id+"F21.imprint","IMPRINT",EDGE,{"disambiguationData":[TD([[subQ8,1.0]])],"derivedFrom":subQ7}),1.0]])]});}
            var Q1;
            {var subQ0=sQuery(id+"F21.wireOp",EDGE,"E28");var subQ1=sQuery(id+"F18.wireOp",EDGE,"E27");var subQ2=sQuery(id+"F18.wireOp",EDGE,"E26");var subQ3=makeQuery(id+"F19.opExtrude","CAP_FACE",FACE,{"disambiguationData":[OSD([subQ2,subQ1])],"isStart":true});var subQ4=subQ3;var subQ7=makeQuery(id+"F20.opFillet","BLEND_EDGE",EDGE,{"blendedFrom":[makeQuery(id+"F19.opExtrude","CAP_EDGE",EDGE,{"disambiguationData":[OSD([subQ2])],"isStart":true}),subQ4],"blendedInto":[subQ4]});var subQ8=makeQuery(id+"F21.imprint","INTERSECT",VERTEX,{"derivedFrom":[subQ7,subQ0]});Q1=makeQuery(id+"F21.imprint","IMPRINT",FACE,{"disambiguationData":[TD([[makeQuery(id+"F21.imprint","IMPRINT",EDGE,{"disambiguationData":[TD([[subQ8,-1.0]])],"derivedFrom":subQ7}),1.0]])]});}
            var Q2;
            {var subQ6=sQuery(id+"F21.wireOp",EDGE,"E38");Q2=makeQuery(id+"F21.imprint","IMPRINT",FACE,{"disambiguationData":[TD([[makeQuery(id+"F21.imprint","IMPRINT",EDGE,{"derivedFrom":subQ6}),1.0]])]});}
            var Q3;
            {var subQ0=sQuery(id+"F21.wireOp",EDGE,"E37");var subQ6=sQuery(id+"F21.wireOp",EDGE,"E34");var subQ7=makeQuery(id+"F21.imprint","INTERSECT",VERTEX,{"derivedFrom":[subQ6,subQ0]});Q3=makeQuery(id+"F21.imprint","IMPRINT",FACE,{"disambiguationData":[TD([[makeQuery(id+"F21.imprint","IMPRINT",EDGE,{"disambiguationData":[TD([[subQ7,-1.0]])],"derivedFrom":subQ0}),-1.0]])]});}
            var Q4;
            {var subQ0=sQuery(id+"F21.wireOp",EDGE,"E37");var subQ6=sQuery(id+"F21.wireOp",EDGE,"E33");var subQ7=makeQuery(id+"F21.imprint","INTERSECT",VERTEX,{"derivedFrom":[subQ6,subQ0]});Q4=makeQuery(id+"F21.imprint","IMPRINT",FACE,{"disambiguationData":[TD([[makeQuery(id+"F21.imprint","IMPRINT",EDGE,{"disambiguationData":[TD([[subQ7,1.0]])],"derivedFrom":subQ0}),-1.0]])]});}
            extrude(context, id + "F22", {"entities" : qUnion([Q0, Q1, Q2, Q3, Q4]), "operationType" : NewBodyOperationType.REMOVE, "oppositeDirection" : true, "depth" : 13 * mm});
        }
        {
            var Q0;
            Q0=makeQuery(id+"F22.boolean.opBoolean","COPY",FACE,{"derivedFrom":makeQuery(id+"F22.opExtrude","SWEPT_FACE",FACE,{"disambiguationData":[OSD([sQuery(id+"F21.wireOp",EDGE,"E33")])]})});
            var sketch = newSketch(context, id + "F23", { "sketchPlane" : qUnion([Q0])});
            skLineSegment(sketch, "E39.bottom", {"start": v(-6.5, 40.1) * mm, "end": v(-14.5, 40.1) * mm});
            skLineSegment(sketch, "E39.top", {"start": v(-6.5, 27.1) * mm, "end": v(-14.5, 27.1) * mm});
            skLineSegment(sketch, "E39.left", {"start": v(-6.5, 40.1) * mm, "end": v(-6.5, 27.1) * mm});
            skLineSegment(sketch, "E39.right", {"start": v(-14.5, 40.1) * mm, "end": v(-14.5, 27.1) * mm});
            skCircle(sketch, "E40", {"center": v(-10.5, 33.6) * mm, "radius": 1.5 * mm});
            skSolve(sketch);
        }
        {
            var Q0;
            Q0=makeQuery(id+"F23.imprint","IMPRINT",FACE,{"disambiguationData":[TD([[makeQuery(id+"F23.imprint","IMPRINT",EDGE,{"derivedFrom":sQuery(id+"F23.wireOp",EDGE,"E40")}),1.0]])]});
            extrude(context, id + "F24", {"entities" : qUnion([Q0]), "operationType" : NewBodyOperationType.REMOVE, "oppositeDirection" : true, "depth" : 25 * mm, "symmetric" : true});
        }
        {
            var Q0;
            Q0=makeQuery(id+"F22.boolean.opBoolean","COPY",FACE,{"derivedFrom":makeQuery(id+"F22.opExtrude","SWEPT_FACE",FACE,{"disambiguationData":[OSD([sQuery(id+"F21.wireOp",EDGE,"E33")])]})});
            cPlane(context, id + "F25", {"entities" : qUnion([Q0]), "cplaneType" : CPlaneType.OFFSET, "offset" : 5 * mm, "width" : 150 * mm, "height" : 150 * mm});
        }
        {
            var Q0;
            Q0=qCreatedBy(id+"F25.planeOp",FACE);
            var sketch = newSketch(context, id + "F26", { "sketchPlane" : qUnion([Q0])});
            skCircle(sketch, "E41", {"center": v(-10.44, 33.6) * mm, "radius": 2.5 * mm});
            skSolve(sketch);
        }
        {
            var Q0;
            Q0=makeQuery(id+"F26.imprint","IMPRINT",FACE,{"disambiguationData":[TD([[makeQuery(id+"F26.imprint","IMPRINT",EDGE,{"derivedFrom":sQuery(id+"F26.wireOp",EDGE,"E41")}),1.0]])]});
            extrude(context, id + "F27", {"entities" : qUnion([Q0]), "operationType" : NewBodyOperationType.REMOVE, "depth" : 25 * mm});
        }
    });
